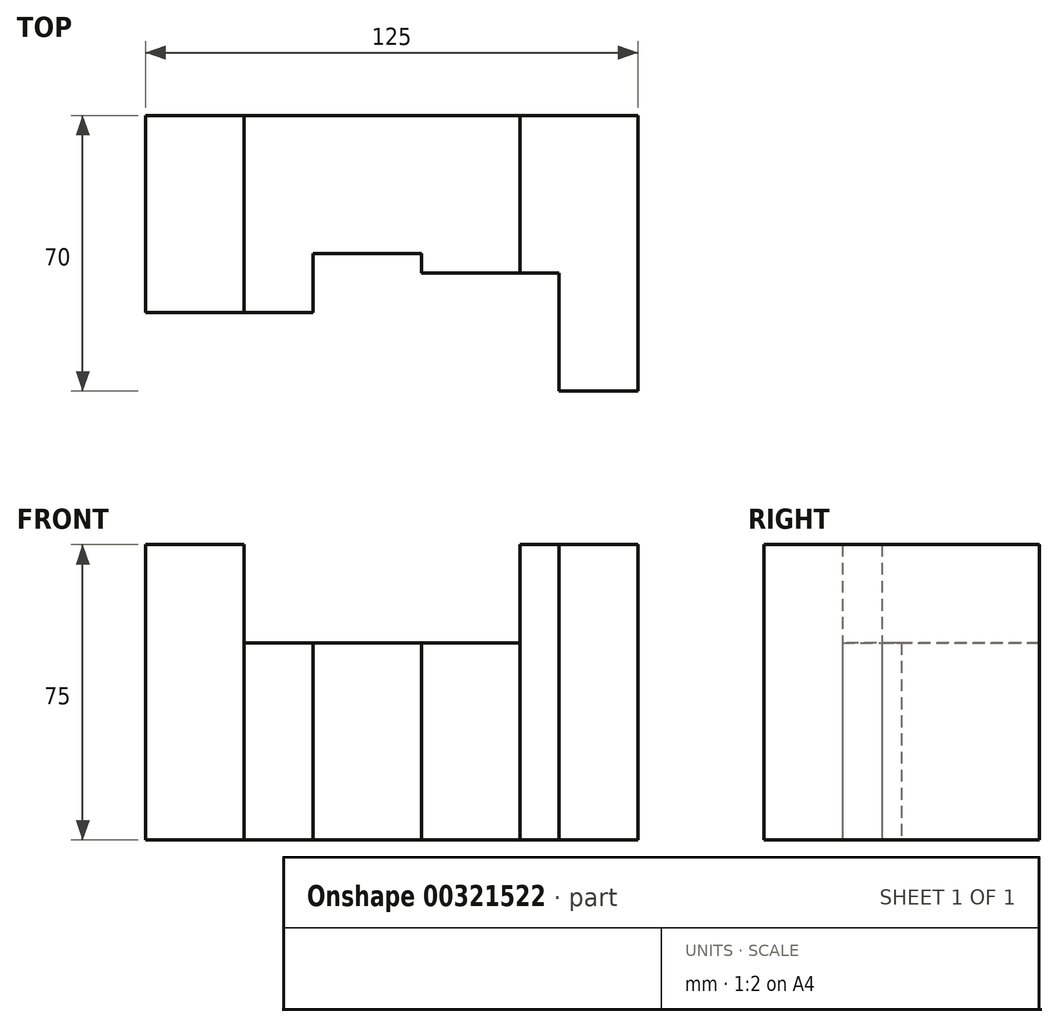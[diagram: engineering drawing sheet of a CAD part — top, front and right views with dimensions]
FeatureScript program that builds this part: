
annotation { "Feature Type Name" : "Feature", "Feature Type Description" : "" }
export const myFeature = defineFeature(function(context is Context, id is Id, definition is map)
    precondition{}
    {
        {
            var Q0;
            Q0=qCreatedBy(makeId("Top.planeOp"),FACE);
            var sketch = newSketch(context, id + "F0", { "sketchPlane" : qUnion([Q0])});
            skLineSegment(sketch, "E0", {"start": v(0, 0) * mm, "end": v(0, 50) * mm});
            skLineSegment(sketch, "E1", {"start": v(0, 50) * mm, "end": v(25, 50) * mm});
            skLineSegment(sketch, "E2", {"start": v(25, 50) * mm, "end": v(25, 0) * mm});
            skLineSegment(sketch, "E3", {"start": v(25, 0) * mm, "end": v(0, 0) * mm});
            skLineSegment(sketch, "E4", {"start": v(25, 0) * mm, "end": v(42.5, 0) * mm});
            skLineSegment(sketch, "E5", {"start": v(42.5, 0) * mm, "end": v(42.5, 15) * mm});
            skLineSegment(sketch, "E6", {"start": v(42.5, 15) * mm, "end": v(70, 15) * mm});
            skLineSegment(sketch, "E7", {"start": v(70, 15) * mm, "end": v(70, 10) * mm});
            skLineSegment(sketch, "E8", {"start": v(70, 10) * mm, "end": v(95, 10) * mm});
            skLineSegment(sketch, "E9", {"start": v(95, 10) * mm, "end": v(105, 10) * mm});
            skLineSegment(sketch, "E10", {"start": v(105, 10) * mm, "end": v(105, -20) * mm});
            skLineSegment(sketch, "E11", {"start": v(105, -20) * mm, "end": v(125, -20) * mm});
            skLineSegment(sketch, "E12", {"start": v(125, -20) * mm, "end": v(125, 50) * mm});
            skLineSegment(sketch, "E13", {"start": v(125, 50) * mm, "end": v(25, 50) * mm});
            skLineSegment(sketch, "E14", {"start": v(95, 10) * mm, "end": v(95, 50) * mm});
            skSolve(sketch);
        }
        {
            var Q0;
            Q0=makeQuery(id+"F0.imprint","IMPRINT",FACE,{"disambiguationData":[TD([[makeQuery(id+"F0.imprint","IMPRINT",EDGE,{"derivedFrom":sQuery(id+"F0.wireOp",EDGE,"E0")}),-1.0]])]});
            var Q1;
            Q1=makeQuery(id+"F0.imprint","IMPRINT",FACE,{"disambiguationData":[TD([[makeQuery(id+"F0.imprint","IMPRINT",EDGE,{"derivedFrom":sQuery(id+"F0.wireOp",EDGE,"E9")}),1.0]])]});
            extrude(context, id + "F1", {"entities" : qUnion([Q0, Q1]), "depth" : 75 * mm});
        }
        {
            var Q0;
            {var subQ1=sQuery(id+"F0.wireOp",EDGE,"E2");Q0=makeQuery(id+"F0.imprint","IMPRINT",FACE,{"disambiguationData":[TD([[makeQuery(id+"F0.imprint","IMPRINT",EDGE,{"derivedFrom":subQ1}),1.0]])]});}
            extrude(context, id + "F2", {"entities" : qUnion([Q0]), "depth" : 50 * mm});
        }
    });
